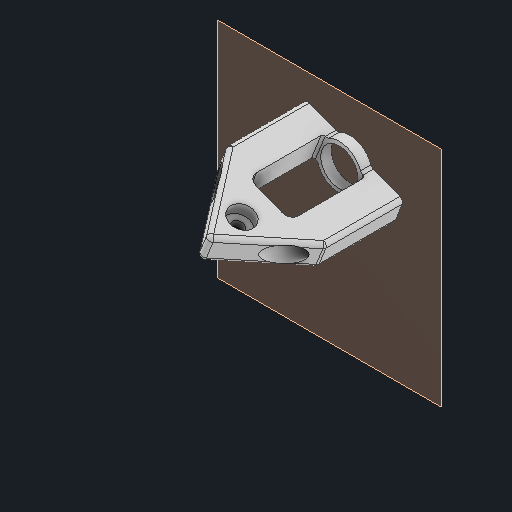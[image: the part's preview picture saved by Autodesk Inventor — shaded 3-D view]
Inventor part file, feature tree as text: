
AUTODESK INVENTOR PART (.ipt)
format: ipt  version: 2024.2 (Build 282272000, 272)  size: 352,256 bytes
history: native  units: in
note: dims shown in document units (in); Inventor stores cm internally (conversion verified against a paired STEP export)
features: extrude x7, sketch x6, fillet x6, other x5, reference x4, plane x3, projected_geometry x2
ambient origin geometry x8: Origin, YZ Plane, XZ Plane, XY Plane, X Axis, Y Axis, Z Axis, Center Point
bodies: Solid1 (feature_tree)
feature tree (33):
  sketch  "Sketch1"  dims[d0=0.1969in d1=0.1969in]
  plane  "Work Plane1"
  extrude  "Extrusion1"  Depth=0.1969in
  extrude  "Extrusion2"  Depth=0.7874in
  extrude  "Extrusion3"  TaperAngle=0.0deg  [1 undecoded]
  plane  "Work Plane2"
  extrude  "Extrusion4"  Depth=0.0394in
  extrude  "Extrusion5"  Depth=1.0in TaperAngle=0.0deg
  fillet  "Fillet1"  Radius=0.629in
  fillet  "Fillet2"  Radius=0.1083in
  fillet  "Fillet3"  Radius=0.1693in
  fillet  "Fillet4"  Radius=0.3543in
  fillet  "Fillet5"  [1 undecoded]
  fillet  "Fillet6"  Radius=0.1181in
  plane  "Work Plane3"
  sketch  "Sketch6"  dims[d27=0.125in d28=0.0312in d29=0.0625in d30=0.0625in d31=0.0625in d32=0.0625in d33=0.1693in d34=0.315in d35=0.0in d36=0.2362in d37=0.0in d38=0.0in d39=0.0in d40=0.9413in d41=0.0in]
  extrude  "Extrusion6"  Depth=0.9413in
  extrude  "Extrusion7"  Depth=0.0625in
  reference  "Reference1"
  reference  "Reference2"
  reference  "Reference3"
  sketch  "Sketch2"  dims[d2=0.7874in d3=0.7874in]
  sketch  "Sketch3"  dims[d4=0.0in d5=0.0in]
  sketch  "Sketch4"  dims[d6=1.0in d7=0.0in d8=0.0394in]
  reference  "Reference4"
  sketch  "Sketch5"  dims[d10=1.0in d11=0.0in d16=1.0in d17=0.0in d19=0.629in d20=0.1083in d21=0.0in d22=0.1693in d23=0.3543in d24=0.0in d25=0.0in d26=0.1181in]
  other  "<userpath>\Desktop\Robotics\Swerve2\Assemblies\Pod.iam"
  other  "Pod.iam"
  other  "Wheel_Base:1"
  projected_geometry  "Project Cut Edges1"
  projected_geometry  "Project Cut Edges2"
  other  "2106 Series Stainless Steel REX Shaft (8mm Diameter, 40mm Length):1"
  other  "Inner_Pod_Holder:1"
note: 2 required parameter values undecoded (feature->parameter linkage not recoverable at this tier; creation-order binding heuristic only, values carry confidence <= 0.55)
